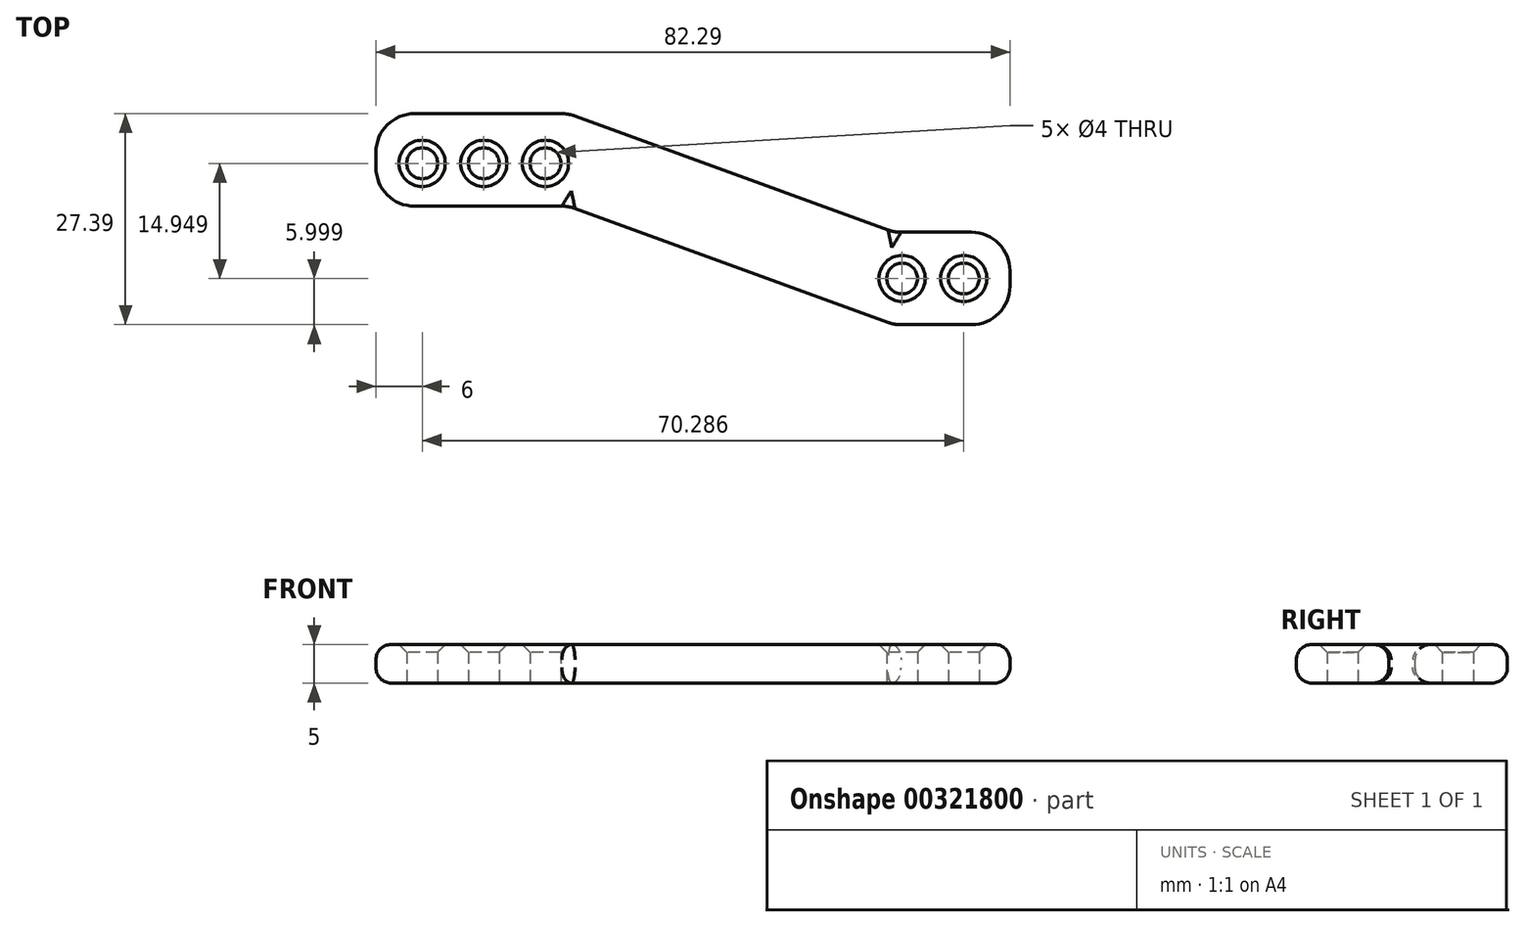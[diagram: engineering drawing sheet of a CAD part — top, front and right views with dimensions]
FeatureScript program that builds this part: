
annotation { "Feature Type Name" : "Feature", "Feature Type Description" : "" }
export const myFeature = defineFeature(function(context is Context, id is Id, definition is map)
    precondition{}
    {
        {
            var Q0;
            Q0=qCreatedBy(makeId("Top.planeOp"),FACE);
            var sketch = newSketch(context, id + "F0", { "sketchPlane" : qUnion([Q0])});
            skLineSegment(sketch, "E0.bottom", {"start": v(0, 0) * mm, "end": v(25, 0) * mm});
            skLineSegment(sketch, "E0.top", {"start": v(0, -12) * mm, "end": v(25, -12) * mm});
            skLineSegment(sketch, "E0.left", {"start": v(0, 0) * mm, "end": v(0, -12) * mm});
            skLineSegment(sketch, "E0.right", {"start": v(25, 0) * mm, "end": v(25, -12) * mm});
            skLineSegment(sketch, "E1", {"start": v(25, -12) * mm, "end": v(67.29, -27.4) * mm});
            skLineSegment(sketch, "E2", {"start": v(25, 0) * mm, "end": v(67.29, -15.4) * mm});
            skLineSegment(sketch, "E3", {"start": v(67.29, -15.4) * mm, "end": v(67.29, -27.4) * mm});
            skLineSegment(sketch, "E4.bottom", {"start": v(67.29, -27.4) * mm, "end": v(82.29, -27.4) * mm});
            skLineSegment(sketch, "E4.top", {"start": v(67.29, -15.4) * mm, "end": v(82.29, -15.4) * mm});
            skLineSegment(sketch, "E4.left", {"start": v(67.29, -27.4) * mm, "end": v(67.29, -15.4) * mm});
            skLineSegment(sketch, "E4.right", {"start": v(82.29, -27.4) * mm, "end": v(82.29, -15.4) * mm});
            skSolve(sketch);
        }
        {
            var Q0;
            Q0 = qSketchRegion(id + "F0", true);
            extrude(context, id + "F1", {"entities" : qUnion([Q0]), "depth" : 5 * mm});
        }
        {
            var Q0;
            Q0=qCreatedBy(makeId("Top.planeOp"),FACE);
            var sketch = newSketch(context, id + "F2", { "sketchPlane" : qUnion([Q0])});
            skCircle(sketch, "E5", {"center": v(6, -6.44) * mm, "radius": 2 * mm});
            skCircle(sketch, "E6", {"center": v(76.29, -21.4) * mm, "radius": 2 * mm});
            skCircle(sketch, "E7.1.0.0", {"center": v(68.29, -21.4) * mm, "radius": 2 * mm});
            skLineSegment(sketch, "E7.direction1", {"start": v(76.29, -21.4) * mm, "end": v(68.29, -21.4) * mm, "construction": true});
            skCircle(sketch, "E8.1.0.0", {"center": v(14, -6.44) * mm, "radius": 2 * mm});
            skCircle(sketch, "E8.2.0.0", {"center": v(22, -6.44) * mm, "radius": 2 * mm});
            skLineSegment(sketch, "E8.direction1", {"start": v(6, -6.44) * mm, "end": v(14, -6.44) * mm, "construction": true});
            skSolve(sketch);
        }
        {
            var Q0;
            Q0 = qSketchRegion(id + "F2", true);
            extrude(context, id + "F3", {"entities" : qUnion([Q0]), "operationType" : NewBodyOperationType.REMOVE, "endBound" : BoundingType.THROUGH_ALL, "depth" : 25 * mm});
        }
        {
            var Q0;
            Q0=makeQuery(id+"F1.opExtrude","CAP_EDGE",EDGE,{"disambiguationData":[OSD([sQuery(id+"F0.wireOp",EDGE,"E0.left")])],"isStart":false});
            var Q1;
            Q1=makeQuery(id+"F1.opExtrude","CAP_EDGE",EDGE,{"disambiguationData":[OSD([sQuery(id+"F0.wireOp",EDGE,"E0.top")])],"isStart":false});
            var Q2;
            Q2=makeQuery(id+"F1.opExtrude","CAP_EDGE",EDGE,{"disambiguationData":[OSD([sQuery(id+"F0.wireOp",EDGE,"E0.bottom")])],"isStart":false});
            var Q3;
            Q3=makeQuery(id+"F1.opExtrude","CAP_EDGE",EDGE,{"disambiguationData":[OSD([sQuery(id+"F0.wireOp",EDGE,"E2")])],"isStart":false});
            var Q4;
            Q4=makeQuery(id+"F1.opExtrude","CAP_EDGE",EDGE,{"disambiguationData":[OSD([sQuery(id+"F0.wireOp",EDGE,"E1")])],"isStart":false});
            var Q5;
            Q5=makeQuery(id+"F1.opExtrude","CAP_EDGE",EDGE,{"disambiguationData":[OSD([sQuery(id+"F0.wireOp",EDGE,"E4.top")])],"isStart":false});
            var Q6;
            Q6=makeQuery(id+"F1.opExtrude","CAP_EDGE",EDGE,{"disambiguationData":[OSD([sQuery(id+"F0.wireOp",EDGE,"E4.bottom")])],"isStart":false});
            var Q7;
            Q7=makeQuery(id+"F1.opExtrude","CAP_EDGE",EDGE,{"disambiguationData":[OSD([sQuery(id+"F0.wireOp",EDGE,"E4.right")])],"isStart":false});
            var Q8;
            Q8=makeQuery(id+"F1.opExtrude","CAP_EDGE",EDGE,{"disambiguationData":[OSD([sQuery(id+"F0.wireOp",EDGE,"E4.right")])],"isStart":true});
            var Q9;
            Q9=makeQuery(id+"F1.opExtrude","CAP_EDGE",EDGE,{"disambiguationData":[OSD([sQuery(id+"F0.wireOp",EDGE,"E4.top")])],"isStart":true});
            var Q10;
            Q10=makeQuery(id+"F1.opExtrude","CAP_EDGE",EDGE,{"disambiguationData":[OSD([sQuery(id+"F0.wireOp",EDGE,"E4.bottom")])],"isStart":true});
            var Q11;
            Q11=makeQuery(id+"F1.opExtrude","CAP_EDGE",EDGE,{"disambiguationData":[OSD([sQuery(id+"F0.wireOp",EDGE,"E1")])],"isStart":true});
            var Q12;
            Q12=makeQuery(id+"F1.opExtrude","CAP_EDGE",EDGE,{"disambiguationData":[OSD([sQuery(id+"F0.wireOp",EDGE,"E2")])],"isStart":true});
            var Q13;
            Q13=makeQuery(id+"F1.opExtrude","CAP_EDGE",EDGE,{"disambiguationData":[OSD([sQuery(id+"F0.wireOp",EDGE,"E0.bottom")])],"isStart":true});
            var Q14;
            Q14=makeQuery(id+"F1.opExtrude","CAP_EDGE",EDGE,{"disambiguationData":[OSD([sQuery(id+"F0.wireOp",EDGE,"E0.top")])],"isStart":true});
            var Q15;
            Q15=makeQuery(id+"F1.opExtrude","CAP_EDGE",EDGE,{"disambiguationData":[OSD([sQuery(id+"F0.wireOp",EDGE,"E0.left")])],"isStart":true});
            fillet(context, id + "F4", {"entities" : qUnion([Q0, Q1, Q2, Q3, Q4, Q5, Q6, Q7, Q8, Q9, Q10, Q11, Q12, Q13, Q14, Q15]), "radius" : 2 * mm, "tangentPropagation" : true, "allowEdgeOverflow" : false});
        }
        {
            var Q0;
            Q0=makeQuery(id+"F1.opExtrude","SWEPT_EDGE",EDGE,{"disambiguationData":[OSD([sQuery(id+"F0.wireOp",EDGE,"E0.bottom"),sQuery(id+"F0.wireOp",EDGE,"E0.left")])]});
            var Q1;
            Q1=makeQuery(id+"F1.opExtrude","SWEPT_EDGE",EDGE,{"disambiguationData":[OSD([sQuery(id+"F0.wireOp",EDGE,"E0.top"),sQuery(id+"F0.wireOp",EDGE,"E0.left")])]});
            var Q2;
            Q2=makeQuery(id+"F1.opExtrude","SWEPT_EDGE",EDGE,{"disambiguationData":[OSD([sQuery(id+"F0.wireOp",EDGE,"E0.bottom"),sQuery(id+"F0.wireOp",EDGE,"E0.right"),sQuery(id+"F0.wireOp",EDGE,"E2")])]});
            var Q3;
            Q3=makeQuery(id+"F1.opExtrude","SWEPT_EDGE",EDGE,{"disambiguationData":[OSD([sQuery(id+"F0.wireOp",EDGE,"E0.top"),sQuery(id+"F0.wireOp",EDGE,"E0.right"),sQuery(id+"F0.wireOp",EDGE,"E1")])]});
            var Q4;
            Q4=makeQuery(id+"F1.opExtrude","SWEPT_EDGE",EDGE,{"disambiguationData":[OSD([sQuery(id+"F0.wireOp",EDGE,"E2"),sQuery(id+"F0.wireOp",EDGE,"E4.top"),sQuery(id+"F0.wireOp",EDGE,"E4.left")])]});
            var Q5;
            Q5=makeQuery(id+"F1.opExtrude","SWEPT_EDGE",EDGE,{"disambiguationData":[OSD([sQuery(id+"F0.wireOp",EDGE,"E1"),sQuery(id+"F0.wireOp",EDGE,"E4.bottom"),sQuery(id+"F0.wireOp",EDGE,"E4.left")])]});
            var Q6;
            Q6=makeQuery(id+"F1.opExtrude","SWEPT_EDGE",EDGE,{"disambiguationData":[OSD([sQuery(id+"F0.wireOp",EDGE,"E4.top"),sQuery(id+"F0.wireOp",EDGE,"E4.right")])]});
            var Q7;
            Q7=makeQuery(id+"F1.opExtrude","SWEPT_EDGE",EDGE,{"disambiguationData":[OSD([sQuery(id+"F0.wireOp",EDGE,"E4.bottom"),sQuery(id+"F0.wireOp",EDGE,"E4.right")])]});
            fillet(context, id + "F5", {"entities" : qUnion([Q0, Q1, Q2, Q3, Q4, Q5, Q6, Q7]), "radius" : 5 * mm, "tangentPropagation" : true, "allowEdgeOverflow" : false});
        }
        {
            var Q0;
            Q0=makeQuery(id+"F3.boolean.opBoolean","INTERSECT",EDGE,{"derivedFrom":[makeQuery(id+"F1.opExtrude","CAP_FACE",FACE,{"disambiguationData":[OSD([sQuery(id+"F0.wireOp",EDGE,"E0.bottom"),sQuery(id+"F0.wireOp",EDGE,"E0.top"),sQuery(id+"F0.wireOp",EDGE,"E0.left"),sQuery(id+"F0.wireOp",EDGE,"E1"),sQuery(id+"F0.wireOp",EDGE,"E2"),sQuery(id+"F0.wireOp",EDGE,"E4.bottom"),sQuery(id+"F0.wireOp",EDGE,"E4.top"),sQuery(id+"F0.wireOp",EDGE,"E4.right")])],"isStart":false}),makeQuery(id+"F3.opExtrude","SWEPT_FACE",FACE,{"disambiguationData":[OSD([sQuery(id+"F2.wireOp",EDGE,"E5")])]})]});
            var Q1;
            Q1=makeQuery(id+"F3.boolean.opBoolean","INTERSECT",EDGE,{"derivedFrom":[makeQuery(id+"F1.opExtrude","CAP_FACE",FACE,{"disambiguationData":[OSD([sQuery(id+"F0.wireOp",EDGE,"E0.bottom"),sQuery(id+"F0.wireOp",EDGE,"E0.top"),sQuery(id+"F0.wireOp",EDGE,"E0.left"),sQuery(id+"F0.wireOp",EDGE,"E1"),sQuery(id+"F0.wireOp",EDGE,"E2"),sQuery(id+"F0.wireOp",EDGE,"E4.bottom"),sQuery(id+"F0.wireOp",EDGE,"E4.top"),sQuery(id+"F0.wireOp",EDGE,"E4.right")])],"isStart":false}),makeQuery(id+"F3.opExtrude","SWEPT_FACE",FACE,{"disambiguationData":[OSD([sQuery(id+"F2.wireOp",EDGE,"E8.1.0.0")])]})]});
            var Q2;
            Q2=makeQuery(id+"F3.boolean.opBoolean","INTERSECT",EDGE,{"derivedFrom":[makeQuery(id+"F1.opExtrude","CAP_FACE",FACE,{"disambiguationData":[OSD([sQuery(id+"F0.wireOp",EDGE,"E0.bottom"),sQuery(id+"F0.wireOp",EDGE,"E0.top"),sQuery(id+"F0.wireOp",EDGE,"E0.left"),sQuery(id+"F0.wireOp",EDGE,"E1"),sQuery(id+"F0.wireOp",EDGE,"E2"),sQuery(id+"F0.wireOp",EDGE,"E4.bottom"),sQuery(id+"F0.wireOp",EDGE,"E4.top"),sQuery(id+"F0.wireOp",EDGE,"E4.right")])],"isStart":false}),makeQuery(id+"F3.opExtrude","SWEPT_FACE",FACE,{"disambiguationData":[OSD([sQuery(id+"F2.wireOp",EDGE,"E8.2.0.0")])]})]});
            var Q3;
            Q3=makeQuery(id+"F3.boolean.opBoolean","INTERSECT",EDGE,{"derivedFrom":[makeQuery(id+"F1.opExtrude","CAP_FACE",FACE,{"disambiguationData":[OSD([sQuery(id+"F0.wireOp",EDGE,"E0.bottom"),sQuery(id+"F0.wireOp",EDGE,"E0.top"),sQuery(id+"F0.wireOp",EDGE,"E0.left"),sQuery(id+"F0.wireOp",EDGE,"E1"),sQuery(id+"F0.wireOp",EDGE,"E2"),sQuery(id+"F0.wireOp",EDGE,"E4.bottom"),sQuery(id+"F0.wireOp",EDGE,"E4.top"),sQuery(id+"F0.wireOp",EDGE,"E4.right")])],"isStart":false}),makeQuery(id+"F3.opExtrude","SWEPT_FACE",FACE,{"disambiguationData":[OSD([sQuery(id+"F2.wireOp",EDGE,"E7.1.0.0")])]})]});
            var Q4;
            Q4=makeQuery(id+"F3.boolean.opBoolean","INTERSECT",EDGE,{"derivedFrom":[makeQuery(id+"F1.opExtrude","CAP_FACE",FACE,{"disambiguationData":[OSD([sQuery(id+"F0.wireOp",EDGE,"E0.bottom"),sQuery(id+"F0.wireOp",EDGE,"E0.top"),sQuery(id+"F0.wireOp",EDGE,"E0.left"),sQuery(id+"F0.wireOp",EDGE,"E1"),sQuery(id+"F0.wireOp",EDGE,"E2"),sQuery(id+"F0.wireOp",EDGE,"E4.bottom"),sQuery(id+"F0.wireOp",EDGE,"E4.top"),sQuery(id+"F0.wireOp",EDGE,"E4.right")])],"isStart":false}),makeQuery(id+"F3.opExtrude","SWEPT_FACE",FACE,{"disambiguationData":[OSD([sQuery(id+"F2.wireOp",EDGE,"E6")])]})]});
            chamfer(context, id + "F6", {"entities" : qUnion([Q0, Q1, Q2, Q3, Q4]), "width" : 1 * mm, "tangentPropagation" : true});
        }
    });
